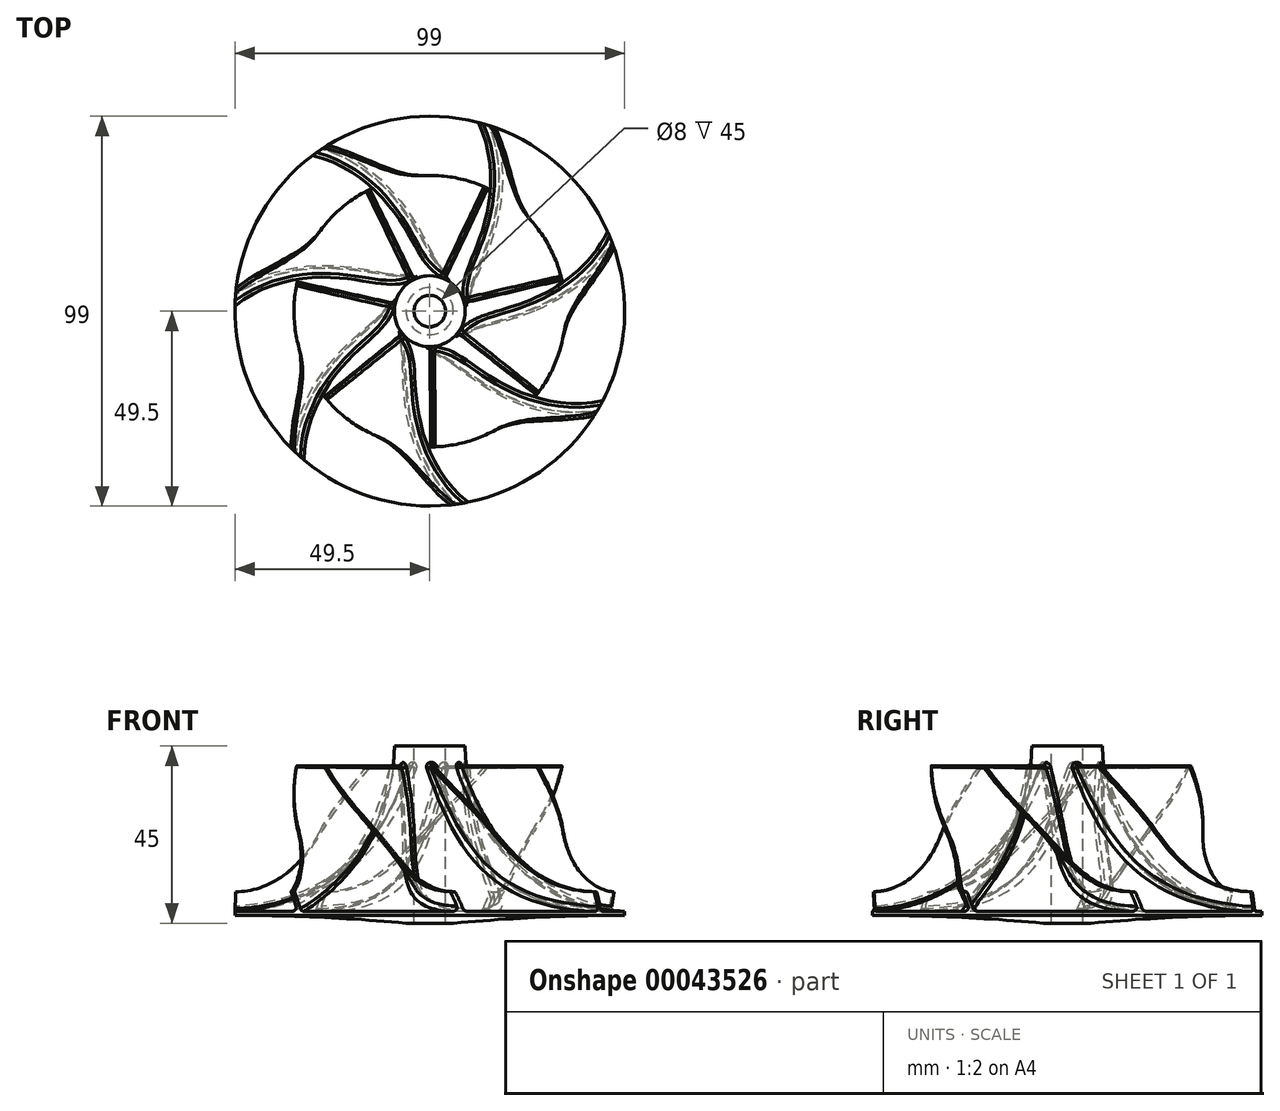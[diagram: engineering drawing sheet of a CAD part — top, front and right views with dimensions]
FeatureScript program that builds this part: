
annotation { "Feature Type Name" : "Feature", "Feature Type Description" : "" }
export const myFeature = defineFeature(function(context is Context, id is Id, definition is map)
    precondition{}
    {
        {
            var Q0;
            Q0=qCreatedBy(makeId("Front.planeOp"),FACE);
            var sketch = newSketch(context, id + "F0", { "sketchPlane" : qUnion([Q0])});
            skLineSegment(sketch, "E0", {"start": v(-4, 0) * mm, "end": v(-4, 45) * mm});
            skLineSegment(sketch, "E1", {"start": v(-4, 0) * mm, "end": v(-6, 0) * mm});
            skLineSegment(sketch, "E2", {"start": v(-6, 0) * mm, "end": v(-6, 2) * mm, "construction": true});
            skLineSegment(sketch, "E3", {"start": v(-6, 2) * mm, "end": v(-49.5, 2) * mm, "construction": true});
            skLineSegment(sketch, "E4", {"start": v(-49.5, 2) * mm, "end": v(-49.5, 3) * mm});
            skLineSegment(sketch, "E5", {"start": v(-4, 45) * mm, "end": v(-9, 45) * mm});
            skLineSegment(sketch, "E6", {"start": v(0, 58.9) * mm, "end": v(0, -58.23) * mm, "construction": true});
            skArc(sketch, "E7", {"start": v(-9, 45) * mm, "mid": v(-20.77, 15.82) * mm, "end": v(-49.5, 3) * mm});
            skArc(sketch, "E8", {"start": v(-6, 0) * mm, "mid": v(-27.73, 1.5) * mm, "end": v(-49.5, 2) * mm});
            skSolve(sketch);
        }
        {
            var Q0;
            Q0=qSketchRegion(id+"F0",true);
            var Q1;
            Q1=sQuery(id+"F0.wireOp",EDGE,"E6");
            revolve(context, id + "F1", {"entities" : qUnion([Q0]), "axis" : qUnion([Q1]), "revolveType" : RevolveType.FULL});
        }
        {
            var Q0;
            Q0=qCreatedBy(makeId("Top.planeOp"),FACE);
            cPlane(context, id + "F2", {"entities" : qUnion([Q0]), "cplaneType" : CPlaneType.OFFSET, "offset" : 40 * mm, "width" : 150 * mm, "height" : 150 * mm});
        }
        {
            var Q0;
            Q0=qCreatedBy(makeId("Top.planeOp"),FACE);
            cPlane(context, id + "F3", {"entities" : qUnion([Q0]), "cplaneType" : CPlaneType.OFFSET, "offset" : 3 * mm, "width" : 150 * mm, "height" : 150 * mm});
        }
        {
            var Q0;
            Q0=qCreatedBy(id+"F2.planeOp",FACE);
            var sketch = newSketch(context, id + "F4", { "sketchPlane" : qUnion([Q0])});
            skArc(sketch, "E9.0", {"start": v(0, -49.5) * mm, "mid": v(0.5, -49.5) * mm, "end": v(1, -49.49) * mm});
            skLineSegment(sketch, "E10", {"start": v(0, -4) * mm, "end": v(0, -49.5) * mm});
            skLineSegment(sketch, "E11.0", {"start": v(1, -4) * mm, "end": v(1, -49.5) * mm});
            skLineSegment(sketch, "E12", {"start": v(0, -4) * mm, "end": v(1, -4) * mm});
            skSolve(sketch);
        }
        {
            var Q0;
            Q0=qCreatedBy(id+"F3.planeOp",FACE);
            var sketch = newSketch(context, id + "F5", { "sketchPlane" : qUnion([Q0])});
            skLineSegment(sketch, "E13", {"start": v(39, 4.4) * mm, "end": v(39, 0) * mm});
            skLineSegment(sketch, "E14", {"start": v(0, 0) * mm, "end": v(14, 0) * mm, "construction": true});
            skLineSegment(sketch, "E15", {"start": v(14, 0) * mm, "end": v(14, 4.4) * mm, "construction": true});
            skCircle(sketch, "E16.0", {"center": v(0, 0) * mm, "radius": 49.5 * mm, "construction": true});
            skLineSegment(sketch, "E17", {"start": v(0, 0) * mm, "end": v(42.87, -24.75) * mm, "construction": true});
            skArc(sketch, "E18", {"start": v(14, 0) * mm, "mid": v(25.54, -21.07) * mm, "end": v(49.5, -22.69) * mm});
            skLineSegment(sketch, "E19", {"start": v(49.5, -21.58) * mm, "end": v(49.5, -22.69) * mm});
            skArc(sketch, "E20.0", {"start": v(15, 0) * mm, "mid": v(26.27, -20.35) * mm, "end": v(49.5, -21.58) * mm});
            skPoint(sketch, "E21.orphan", {"position": v(49.5, 0) * mm});
            skLineSegment(sketch, "E22", {"start": v(14, 0) * mm, "end": v(15, 0) * mm});
            skSolve(sketch);
        }
        {
            var Q1;
            Q1=qSketchRegion(id+"F4",true);
            var Q2;
            Q2=qSketchRegion(id+"F5",true);
            loft(context, id + "F6", {"operationType" : NewBodyOperationType.ADD, "sheetProfilesArray" : [{ "sheetProfileEntities" : qUnion([Q1]) }, { "sheetProfileEntities" : qUnion([Q2]) }]});
        }
        {
            var Q0;
            Q0=qCreatedBy(makeId("Front.planeOp"),FACE);
            var sketch = newSketch(context, id + "F7", { "sketchPlane" : qUnion([Q0])});
            skPoint(sketch, "E23.0", {"position": v(0, 40) * mm});
            skLineSegment(sketch, "E24", {"start": v(0, 40) * mm, "end": v(-9.3, 40) * mm});
            skPoint(sketch, "E25", {"position": v(-34.5, 40) * mm});
            skLineSegment(sketch, "E26", {"start": v(0, 61.5) * mm, "end": v(0, -16.06) * mm, "construction": true});
            skLineSegment(sketch, "E27", {"start": v(-34.5, 40) * mm, "end": v(-34.5, 23) * mm});
            skLineSegment(sketch, "E28", {"start": v(-49.5, 8) * mm, "end": v(-64.35, 8) * mm, "construction": true});
            skLineSegment(sketch, "E29", {"start": v(-49.5, 8) * mm, "end": v(-49.5, 23) * mm, "construction": true});
            skArc(sketch, "E30", {"start": v(-49.5, 3) * mm, "mid": v(-20.77, 15.82) * mm, "end": v(-9, 45) * mm, "construction": true});
            skArc(sketch, "E31", {"start": v(-49.5, 8) * mm, "mid": v(-38.9, 12.4) * mm, "end": v(-34.5, 23) * mm});
            skLineSegment(sketch, "E32.trimOffspring", {"start": v(-34.5, 40) * mm, "end": v(-69.01, 40) * mm});
            skLineSegment(sketch, "E33", {"start": v(-49.5, 8) * mm, "end": v(-49.5, 3) * mm});
            skLineSegment(sketch, "E34", {"start": v(-49.5, 3) * mm, "end": v(-69.01, 3) * mm});
            skLineSegment(sketch, "E35", {"start": v(-69.01, 3) * mm, "end": v(-69.01, 40) * mm});
            skSolve(sketch);
        }
        {
            var Q0;
            Q0=qSketchRegion(id+"F7",true);
            var Q1;
            Q1=sQuery(id+"F7.wireOp",EDGE,"E26");
            revolve(context, id + "F8", {"operationType" : NewBodyOperationType.REMOVE, "entities" : qUnion([Q0]), "axis" : qUnion([Q1]), "revolveType" : RevolveType.FULL, "oppositeDirection" : true});
        }
        {
            var Q0;
            Q0=makeQuery(id+"F6.opLoft","SWEPT_FACE",FACE,{"disambiguationData":[OSD([sQuery(id+"F4.wireOp",EDGE,"E9.0"),sQuery(id+"F4.wireOp",EDGE,"E11.0"),sQuery(id+"F4.wireOp",EDGE,"E12"),sQuery(id+"F5.wireOp",EDGE,"E19"),sQuery(id+"F5.wireOp",EDGE,"E20.0"),sQuery(id+"F5.wireOp",EDGE,"E22")])]});
            var Q1;
            Q1=makeQuery(id+"F8.boolean.opBoolean","COPY",FACE,{"derivedFrom":makeQuery(id+"F8.opRevolve","SWEPT_FACE",FACE,{"disambiguationData":[OSD([sQuery(id+"F7.wireOp",EDGE,"E31")])]})});
            var Q2;
            Q2=makeQuery(id+"F8.boolean.opBoolean","COPY",FACE,{"derivedFrom":makeQuery(id+"F8.opRevolve","SWEPT_FACE",FACE,{"disambiguationData":[OSD([sQuery(id+"F7.wireOp",EDGE,"E27")])]})});
            var Q3;
            {var subQ0=sQuery(id+"F4.wireOp",EDGE,"E9.0");var subQ1=sQuery(id+"F4.wireOp",EDGE,"E10");var subQ2=sQuery(id+"F4.wireOp",EDGE,"E12");var subQ3=sQuery(id+"F5.wireOp",EDGE,"E18");var subQ4=sQuery(id+"F5.wireOp",EDGE,"E19");var subQ5=sQuery(id+"F5.wireOp",EDGE,"E22");Q3=makeQuery(id+"F6.boolean.opBoolean","SPLIT",FACE,{"disambiguationData":[TD([makeQuery(id+"F1.opRevolve","SWEPT_FACE",FACE,{"disambiguationData":[OSD([sQuery(id+"F0.wireOp",EDGE,"E4")])]})])],"derivedFrom":makeQuery(id+"F6.opLoft","SWEPT_FACE",FACE,{"disambiguationData":[OSD([subQ0,subQ1,subQ2,subQ3,subQ4,subQ5])]})});}
            var Q4;
            {var subQ2=sQuery(id+"F4.wireOp",EDGE,"E9.0");Q4=makeQuery(id+"F6.opLoft","CAP_FACE",FACE,{"disambiguationData":[OSD([makeQuery(id+"F4.imprint","IMPRINT",FACE,{"disambiguationData":[TD([[makeQuery(id+"F4.imprint","IMPRINT",EDGE,{"derivedFrom":subQ2}),1.0]])]})])],"isStart":true});}
            var Q5;
            Q5=makeQuery(id+"F1.opRevolve","SWEPT_FACE",FACE,{"disambiguationData":[OSD([sQuery(id+"F0.wireOp",EDGE,"E0")])]});
            circularPattern(context, id + "F9", {"faces" : qUnion([Q0, Q1, Q2, Q3, Q4]), "axis" : qUnion([Q5]), "angle" : 51.43 * degree, "instanceCount" : round(7), "patternType" : PatternType.FACE});
        }
        {
            var Q0;
            Q0=makeQuery(id+"F6.opLoft","MID_CAP_EDGE",EDGE,{"disambiguationData":[OSD([sQuery(id+"F4.wireOp",EDGE,"E9.0"),sQuery(id+"F4.wireOp",EDGE,"E10"),sQuery(id+"F4.wireOp",EDGE,"E12")])],"capPos":0.0});
            var Q1;
            Q1=makeQuery(id+"F9.opPattern","COPY",EDGE,{"derivedFrom":makeQuery(id+"F6.opLoft","MID_CAP_EDGE",EDGE,{"disambiguationData":[OSD([sQuery(id+"F4.wireOp",EDGE,"E9.0"),sQuery(id+"F4.wireOp",EDGE,"E10"),sQuery(id+"F4.wireOp",EDGE,"E12")])],"capPos":0.0}),"instanceName":"1"});
            var Q2;
            Q2=makeQuery(id+"F9.opPattern","COPY",EDGE,{"derivedFrom":makeQuery(id+"F6.opLoft","MID_CAP_EDGE",EDGE,{"disambiguationData":[OSD([sQuery(id+"F4.wireOp",EDGE,"E9.0"),sQuery(id+"F4.wireOp",EDGE,"E10"),sQuery(id+"F4.wireOp",EDGE,"E12")])],"capPos":0.0}),"instanceName":"6"});
            var Q3;
            Q3=makeQuery(id+"F9.opPattern","COPY",EDGE,{"derivedFrom":makeQuery(id+"F6.opLoft","MID_CAP_EDGE",EDGE,{"disambiguationData":[OSD([sQuery(id+"F4.wireOp",EDGE,"E9.0"),sQuery(id+"F4.wireOp",EDGE,"E10"),sQuery(id+"F4.wireOp",EDGE,"E12")])],"capPos":0.0}),"instanceName":"5"});
            var Q4;
            Q4=makeQuery(id+"F9.opPattern","COPY",EDGE,{"derivedFrom":makeQuery(id+"F6.opLoft","MID_CAP_EDGE",EDGE,{"disambiguationData":[OSD([sQuery(id+"F4.wireOp",EDGE,"E9.0"),sQuery(id+"F4.wireOp",EDGE,"E10"),sQuery(id+"F4.wireOp",EDGE,"E12")])],"capPos":0.0}),"instanceName":"4"});
            var Q5;
            Q5=makeQuery(id+"F9.opPattern","COPY",EDGE,{"derivedFrom":makeQuery(id+"F6.opLoft","MID_CAP_EDGE",EDGE,{"disambiguationData":[OSD([sQuery(id+"F4.wireOp",EDGE,"E9.0"),sQuery(id+"F4.wireOp",EDGE,"E10"),sQuery(id+"F4.wireOp",EDGE,"E12")])],"capPos":0.0}),"instanceName":"3"});
            var Q6;
            Q6=makeQuery(id+"F9.opPattern","COPY",EDGE,{"derivedFrom":makeQuery(id+"F6.opLoft","MID_CAP_EDGE",EDGE,{"disambiguationData":[OSD([sQuery(id+"F4.wireOp",EDGE,"E9.0"),sQuery(id+"F4.wireOp",EDGE,"E10"),sQuery(id+"F4.wireOp",EDGE,"E12")])],"capPos":0.0}),"instanceName":"2"});
            fillet(context, id + "F10", {"entities" : qUnion([Q0, Q1, Q2, Q3, Q4, Q5, Q6]), "radius" : .2 * mm, "tangentPropagation" : true, "allowEdgeOverflow" : false});
        }
        {
            var Q0;
            Q0=makeQuery(id+"F9.opPattern","COPY",EDGE,{"derivedFrom":makeQuery(id+"F6.opLoft","MID_CAP_EDGE",EDGE,{"disambiguationData":[OSD([sQuery(id+"F4.wireOp",EDGE,"E9.0"),sQuery(id+"F4.wireOp",EDGE,"E11.0"),sQuery(id+"F4.wireOp",EDGE,"E12")])],"capPos":0.0}),"instanceName":"2"});
            var Q1;
            Q1=makeQuery(id+"F9.opPattern","COPY",EDGE,{"derivedFrom":makeQuery(id+"F6.opLoft","MID_CAP_EDGE",EDGE,{"disambiguationData":[OSD([sQuery(id+"F4.wireOp",EDGE,"E9.0"),sQuery(id+"F4.wireOp",EDGE,"E11.0"),sQuery(id+"F4.wireOp",EDGE,"E12")])],"capPos":0.0}),"instanceName":"1"});
            var Q2;
            Q2=makeQuery(id+"F6.opLoft","MID_CAP_EDGE",EDGE,{"disambiguationData":[OSD([sQuery(id+"F4.wireOp",EDGE,"E9.0"),sQuery(id+"F4.wireOp",EDGE,"E11.0"),sQuery(id+"F4.wireOp",EDGE,"E12")])],"capPos":0.0});
            var Q3;
            Q3=makeQuery(id+"F9.opPattern","COPY",EDGE,{"derivedFrom":makeQuery(id+"F6.opLoft","MID_CAP_EDGE",EDGE,{"disambiguationData":[OSD([sQuery(id+"F4.wireOp",EDGE,"E9.0"),sQuery(id+"F4.wireOp",EDGE,"E11.0"),sQuery(id+"F4.wireOp",EDGE,"E12")])],"capPos":0.0}),"instanceName":"6"});
            var Q4;
            Q4=makeQuery(id+"F9.opPattern","COPY",EDGE,{"derivedFrom":makeQuery(id+"F6.opLoft","MID_CAP_EDGE",EDGE,{"disambiguationData":[OSD([sQuery(id+"F4.wireOp",EDGE,"E9.0"),sQuery(id+"F4.wireOp",EDGE,"E11.0"),sQuery(id+"F4.wireOp",EDGE,"E12")])],"capPos":0.0}),"instanceName":"5"});
            var Q5;
            Q5=makeQuery(id+"F9.opPattern","COPY",EDGE,{"derivedFrom":makeQuery(id+"F6.opLoft","MID_CAP_EDGE",EDGE,{"disambiguationData":[OSD([sQuery(id+"F4.wireOp",EDGE,"E9.0"),sQuery(id+"F4.wireOp",EDGE,"E11.0"),sQuery(id+"F4.wireOp",EDGE,"E12")])],"capPos":0.0}),"instanceName":"4"});
            var Q6;
            Q6=makeQuery(id+"F9.opPattern","COPY",EDGE,{"derivedFrom":makeQuery(id+"F6.opLoft","MID_CAP_EDGE",EDGE,{"disambiguationData":[OSD([sQuery(id+"F4.wireOp",EDGE,"E9.0"),sQuery(id+"F4.wireOp",EDGE,"E11.0"),sQuery(id+"F4.wireOp",EDGE,"E12")])],"capPos":0.0}),"instanceName":"3"});
            fillet(context, id + "F11", {"entities" : qUnion([Q0, Q1, Q2, Q3, Q4, Q5, Q6]), "radius" : 1 * mm, "tangentPropagation" : true, "allowEdgeOverflow" : false});
        }
        {
            var Q0;
            Q0=makeQuery(id+"F9.opPattern","COPY",EDGE,{"derivedFrom":makeQuery(id+"F6.boolean.opBoolean","INTERSECT",EDGE,{"derivedFrom":[makeQuery(id+"F1.opRevolve","SWEPT_FACE",FACE,{"disambiguationData":[OSD([sQuery(id+"F0.wireOp",EDGE,"E7")])]}),makeQuery(id+"F6.opLoft","SWEPT_FACE",FACE,{"disambiguationData":[OSD([sQuery(id+"F4.wireOp",EDGE,"E9.0"),sQuery(id+"F4.wireOp",EDGE,"E10"),sQuery(id+"F4.wireOp",EDGE,"E12"),sQuery(id+"F5.wireOp",EDGE,"E18"),sQuery(id+"F5.wireOp",EDGE,"E19"),sQuery(id+"F5.wireOp",EDGE,"E22")])]})]}),"instanceName":"2"});
            var Q1;
            Q1=makeQuery(id+"F10.opFillet","BLEND_EDGE",EDGE,{"blendedFrom":[makeQuery(id+"F9.opPattern","COPY",EDGE,{"derivedFrom":makeQuery(id+"F6.opLoft","MID_CAP_EDGE",EDGE,{"disambiguationData":[OSD([sQuery(id+"F4.wireOp",EDGE,"E9.0"),sQuery(id+"F4.wireOp",EDGE,"E10"),sQuery(id+"F4.wireOp",EDGE,"E12")])],"capPos":0.0}),"instanceName":"2"}),makeQuery(id+"F1.opRevolve","SWEPT_FACE",FACE,{"disambiguationData":[OSD([sQuery(id+"F0.wireOp",EDGE,"E7")])]})],"blendedInto":[makeQuery(id+"F1.opRevolve","SWEPT_FACE",FACE,{"disambiguationData":[OSD([sQuery(id+"F0.wireOp",EDGE,"E7")])]})]});
            var Q2;
            {var subQ2=sQuery(id+"F4.wireOp",EDGE,"E9.0");Q2=makeQuery(id+"F9.opPattern","COPY",EDGE,{"derivedFrom":makeQuery(id+"F6.boolean.opBoolean","INTERSECT",EDGE,{"derivedFrom":[makeQuery(id+"F1.opRevolve","SWEPT_FACE",FACE,{"disambiguationData":[OSD([sQuery(id+"F0.wireOp",EDGE,"E7")])]}),makeQuery(id+"F6.opLoft","CAP_FACE",FACE,{"disambiguationData":[OSD([makeQuery(id+"F4.imprint","IMPRINT",FACE,{"disambiguationData":[TD([[makeQuery(id+"F4.imprint","IMPRINT",EDGE,{"derivedFrom":subQ2}),1.0]])]})])],"isStart":true})]}),"instanceName":"2"});}
            var Q3;
            Q3=makeQuery(id+"F11.opFillet","BLEND_EDGE",EDGE,{"blendedFrom":[makeQuery(id+"F9.opPattern","COPY",EDGE,{"derivedFrom":makeQuery(id+"F6.opLoft","MID_CAP_EDGE",EDGE,{"disambiguationData":[OSD([sQuery(id+"F4.wireOp",EDGE,"E9.0"),sQuery(id+"F4.wireOp",EDGE,"E11.0"),sQuery(id+"F4.wireOp",EDGE,"E12")])],"capPos":0.0}),"instanceName":"2"}),makeQuery(id+"F1.opRevolve","SWEPT_FACE",FACE,{"disambiguationData":[OSD([sQuery(id+"F0.wireOp",EDGE,"E7")])]})],"blendedInto":[makeQuery(id+"F1.opRevolve","SWEPT_FACE",FACE,{"disambiguationData":[OSD([sQuery(id+"F0.wireOp",EDGE,"E7")])]})]});
            var Q4;
            Q4=makeQuery(id+"F9.opPattern","COPY",EDGE,{"derivedFrom":makeQuery(id+"F6.boolean.opBoolean","INTERSECT",EDGE,{"derivedFrom":[makeQuery(id+"F1.opRevolve","SWEPT_FACE",FACE,{"disambiguationData":[OSD([sQuery(id+"F0.wireOp",EDGE,"E7")])]}),makeQuery(id+"F6.opLoft","SWEPT_FACE",FACE,{"disambiguationData":[OSD([sQuery(id+"F4.wireOp",EDGE,"E9.0"),sQuery(id+"F4.wireOp",EDGE,"E11.0"),sQuery(id+"F4.wireOp",EDGE,"E12"),sQuery(id+"F5.wireOp",EDGE,"E19"),sQuery(id+"F5.wireOp",EDGE,"E20.0"),sQuery(id+"F5.wireOp",EDGE,"E22")])]})]}),"instanceName":"2"});
            var Q5;
            Q5=makeQuery(id+"F9.opPattern","COPY",EDGE,{"derivedFrom":makeQuery(id+"F6.boolean.opBoolean","INTERSECT",EDGE,{"derivedFrom":[makeQuery(id+"F1.opRevolve","SWEPT_FACE",FACE,{"disambiguationData":[OSD([sQuery(id+"F0.wireOp",EDGE,"E7")])]}),makeQuery(id+"F6.opLoft","SWEPT_FACE",FACE,{"disambiguationData":[OSD([sQuery(id+"F4.wireOp",EDGE,"E9.0"),sQuery(id+"F4.wireOp",EDGE,"E10"),sQuery(id+"F4.wireOp",EDGE,"E12"),sQuery(id+"F5.wireOp",EDGE,"E18"),sQuery(id+"F5.wireOp",EDGE,"E19"),sQuery(id+"F5.wireOp",EDGE,"E22")])]})]}),"instanceName":"1"});
            var Q6;
            Q6=makeQuery(id+"F6.boolean.opBoolean","INTERSECT",EDGE,{"derivedFrom":[makeQuery(id+"F1.opRevolve","SWEPT_FACE",FACE,{"disambiguationData":[OSD([sQuery(id+"F0.wireOp",EDGE,"E7")])]}),makeQuery(id+"F6.opLoft","SWEPT_FACE",FACE,{"disambiguationData":[OSD([sQuery(id+"F4.wireOp",EDGE,"E9.0"),sQuery(id+"F4.wireOp",EDGE,"E10"),sQuery(id+"F4.wireOp",EDGE,"E12"),sQuery(id+"F5.wireOp",EDGE,"E18"),sQuery(id+"F5.wireOp",EDGE,"E19"),sQuery(id+"F5.wireOp",EDGE,"E22")])]})]});
            var Q7;
            Q7=makeQuery(id+"F9.opPattern","COPY",EDGE,{"derivedFrom":makeQuery(id+"F6.boolean.opBoolean","INTERSECT",EDGE,{"derivedFrom":[makeQuery(id+"F1.opRevolve","SWEPT_FACE",FACE,{"disambiguationData":[OSD([sQuery(id+"F0.wireOp",EDGE,"E7")])]}),makeQuery(id+"F6.opLoft","SWEPT_FACE",FACE,{"disambiguationData":[OSD([sQuery(id+"F4.wireOp",EDGE,"E9.0"),sQuery(id+"F4.wireOp",EDGE,"E10"),sQuery(id+"F4.wireOp",EDGE,"E12"),sQuery(id+"F5.wireOp",EDGE,"E18"),sQuery(id+"F5.wireOp",EDGE,"E19"),sQuery(id+"F5.wireOp",EDGE,"E22")])]})]}),"instanceName":"6"});
            var Q8;
            Q8=makeQuery(id+"F9.opPattern","COPY",EDGE,{"derivedFrom":makeQuery(id+"F6.boolean.opBoolean","INTERSECT",EDGE,{"derivedFrom":[makeQuery(id+"F1.opRevolve","SWEPT_FACE",FACE,{"disambiguationData":[OSD([sQuery(id+"F0.wireOp",EDGE,"E7")])]}),makeQuery(id+"F6.opLoft","SWEPT_FACE",FACE,{"disambiguationData":[OSD([sQuery(id+"F4.wireOp",EDGE,"E9.0"),sQuery(id+"F4.wireOp",EDGE,"E10"),sQuery(id+"F4.wireOp",EDGE,"E12"),sQuery(id+"F5.wireOp",EDGE,"E18"),sQuery(id+"F5.wireOp",EDGE,"E19"),sQuery(id+"F5.wireOp",EDGE,"E22")])]})]}),"instanceName":"5"});
            var Q9;
            Q9=makeQuery(id+"F9.opPattern","COPY",EDGE,{"derivedFrom":makeQuery(id+"F6.boolean.opBoolean","INTERSECT",EDGE,{"derivedFrom":[makeQuery(id+"F1.opRevolve","SWEPT_FACE",FACE,{"disambiguationData":[OSD([sQuery(id+"F0.wireOp",EDGE,"E7")])]}),makeQuery(id+"F6.opLoft","SWEPT_FACE",FACE,{"disambiguationData":[OSD([sQuery(id+"F4.wireOp",EDGE,"E9.0"),sQuery(id+"F4.wireOp",EDGE,"E10"),sQuery(id+"F4.wireOp",EDGE,"E12"),sQuery(id+"F5.wireOp",EDGE,"E18"),sQuery(id+"F5.wireOp",EDGE,"E19"),sQuery(id+"F5.wireOp",EDGE,"E22")])]})]}),"instanceName":"4"});
            var Q10;
            Q10=makeQuery(id+"F9.opPattern","COPY",EDGE,{"derivedFrom":makeQuery(id+"F6.boolean.opBoolean","INTERSECT",EDGE,{"derivedFrom":[makeQuery(id+"F1.opRevolve","SWEPT_FACE",FACE,{"disambiguationData":[OSD([sQuery(id+"F0.wireOp",EDGE,"E7")])]}),makeQuery(id+"F6.opLoft","SWEPT_FACE",FACE,{"disambiguationData":[OSD([sQuery(id+"F4.wireOp",EDGE,"E9.0"),sQuery(id+"F4.wireOp",EDGE,"E10"),sQuery(id+"F4.wireOp",EDGE,"E12"),sQuery(id+"F5.wireOp",EDGE,"E18"),sQuery(id+"F5.wireOp",EDGE,"E19"),sQuery(id+"F5.wireOp",EDGE,"E22")])]})]}),"instanceName":"3"});
            fillet(context, id + "F12", {"entities" : qUnion([Q0, Q1, Q2, Q3, Q4, Q5, Q6, Q7, Q8, Q9, Q10]), "radius" : 1 * mm, "tangentPropagation" : true, "allowEdgeOverflow" : false});
        }
    });
